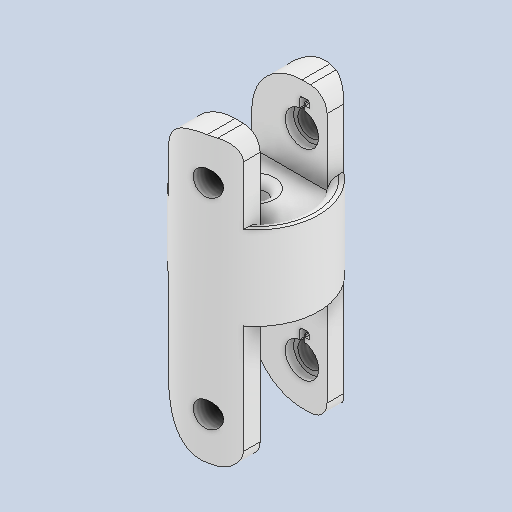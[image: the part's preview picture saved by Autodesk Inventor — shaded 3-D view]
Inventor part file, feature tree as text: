
AUTODESK INVENTOR PART (.ipt)
format: ipt  version: 2022 (Build 260153000, 153)  size: 408,576 bytes
history: native  units: in
note: dims shown in document units (in); Inventor stores cm internally (conversion verified against a paired STEP export)
features: sketch x14, extrude x10, fillet x7, chamfer x4, hole x4, thread x4
ambient origin geometry x8: Origin, YZ Plane, XZ Plane, XY Plane, X Axis, Y Axis, Z Axis, Center Point
bodies: Solid1 (feature_tree)
feature tree (43):
  extrude  "Extrusion1"  Depth=0.1181in
  extrude  "Extrusion2"  Depth=0.0984in
  extrude  "Extrusion3"  Depth=0.3937in TaperAngle=0.0deg
  chamfer  "Chamfer1"  Distance=0.0098in Angle=45.0deg
  extrude  "Extrusion4"  Depth=0.2362in
  fillet  "Fillet1"  Radius=0.0787in
  fillet  "Fillet2"  Radius=0.1969in
  chamfer  "Chamfer2"  Distance=0.0394in
  chamfer  "Chamfer3"  Distance=0.0394in
  hole  "Hole1"  [1 undecoded]
  hole  "Hole2"  [1 undecoded]
  sketch  "Sketch7"  dims[d30=0.1181in d31=0.2362in d32=0.1575in d33=0.0394in d34=90.0deg d35=0.1575in d36=0.0in]
  sketch  "Sketch8"  dims[d37=0.1181in d38=0.2362in d39=0.1575in d40=0.0394in d41=90.0deg d42=0.1575in d43=0.8108in d53=0.0394in d54=0.0in d55=0.0394in d56=0.0in]
  extrude  "Extrusion5"  Depth=0.0394in
  extrude  "Extrusion6"  Depth=0.0394in TaperAngle=45.0deg
  extrude  "Extrusion7"  Depth=0.0394in
  fillet  "Fillet3"  Radius=0.0394in
  fillet  "Fillet4"  Radius=0.0394in
  hole  "Hole3"  [1 undecoded]
  hole  "Hole4"  [1 undecoded]
  chamfer  "Chamfer4"  Distance=0.2362in
  fillet  "Fillet5"  Radius=0.2362in
  fillet  "Fillet6"  Radius=0.2362in
  sketch  "Sketch12"  dims[d70=0.1181in d71=0.2362in d72=0.1575in d73=0.0394in d74=90.0deg d75=0.1575in d76=0.0in d77=0.0394in d78=0.0492in d79=45.0deg]
  extrude  "Extrusion8"  [1 undecoded]
  extrude  "Extrusion9"  [1 undecoded]
  extrude  "Extrusion10"  [1 undecoded]
  fillet  "Fillet7"  [1 undecoded]
  thread  "Thread1"  [1 undecoded]
  thread  "Thread2"  [1 undecoded]
  thread  "Thread3"  [1 undecoded]
  thread  "Thread4"  [1 undecoded]
  sketch  "Sketch1"  dims[d3=0.5906in d4=0.0in d5=0.1181in]
  sketch  "Sketch2"  dims[d6=0.1181in d7=0.0984in]
  sketch  "Sketch3"  dims[d8=0.3937in d9=0.0in d12=0.1575in d13=0.0in d14=0.0098in d15=0.0492in d16=45.0deg]
  sketch  "Sketch4"  dims[d19=0.1575in d20=0.0in d21=0.2362in d22=0.0787in]
  sketch  "Sketch5"  dims[d23=0.0394in d24=0.0492in d25=45.0deg]
  sketch  "Sketch6"  dims[d26=0.0098in d27=0.0492in d28=45.0deg d29=0.1969in]
  sketch  "Sketch9"  dims[d57=0.3543in d58=0.0in d59=0.2362in]
  sketch  "Sketch10"  dims[d60=0.0787in d61=0.1969in]
  sketch  "Sketch11"  dims[d62=0.1181in d63=0.2362in d64=0.1575in d65=0.0394in d66=90.0deg d67=0.1575in d68=0.0in d69=0.1969in]
  sketch  "Sketch13"  dims[d80=0.0394in d81=0.0394in d82=0.0394in d83=0.0in d84=0.0394in d85=0.0in]
  sketch  "Sketch14"  dims[d86=0.0394in d87=0.0in d88=0.0394in d89=0.2362in d90=0.0in d91=0.2362in d92=0.0in d93=0.2362in d94=0.0in d95=0.2362in d96=0.0in]
note: 12 required parameter values undecoded (feature->parameter linkage not recoverable at this tier; creation-order binding heuristic only, values carry confidence <= 0.55)
